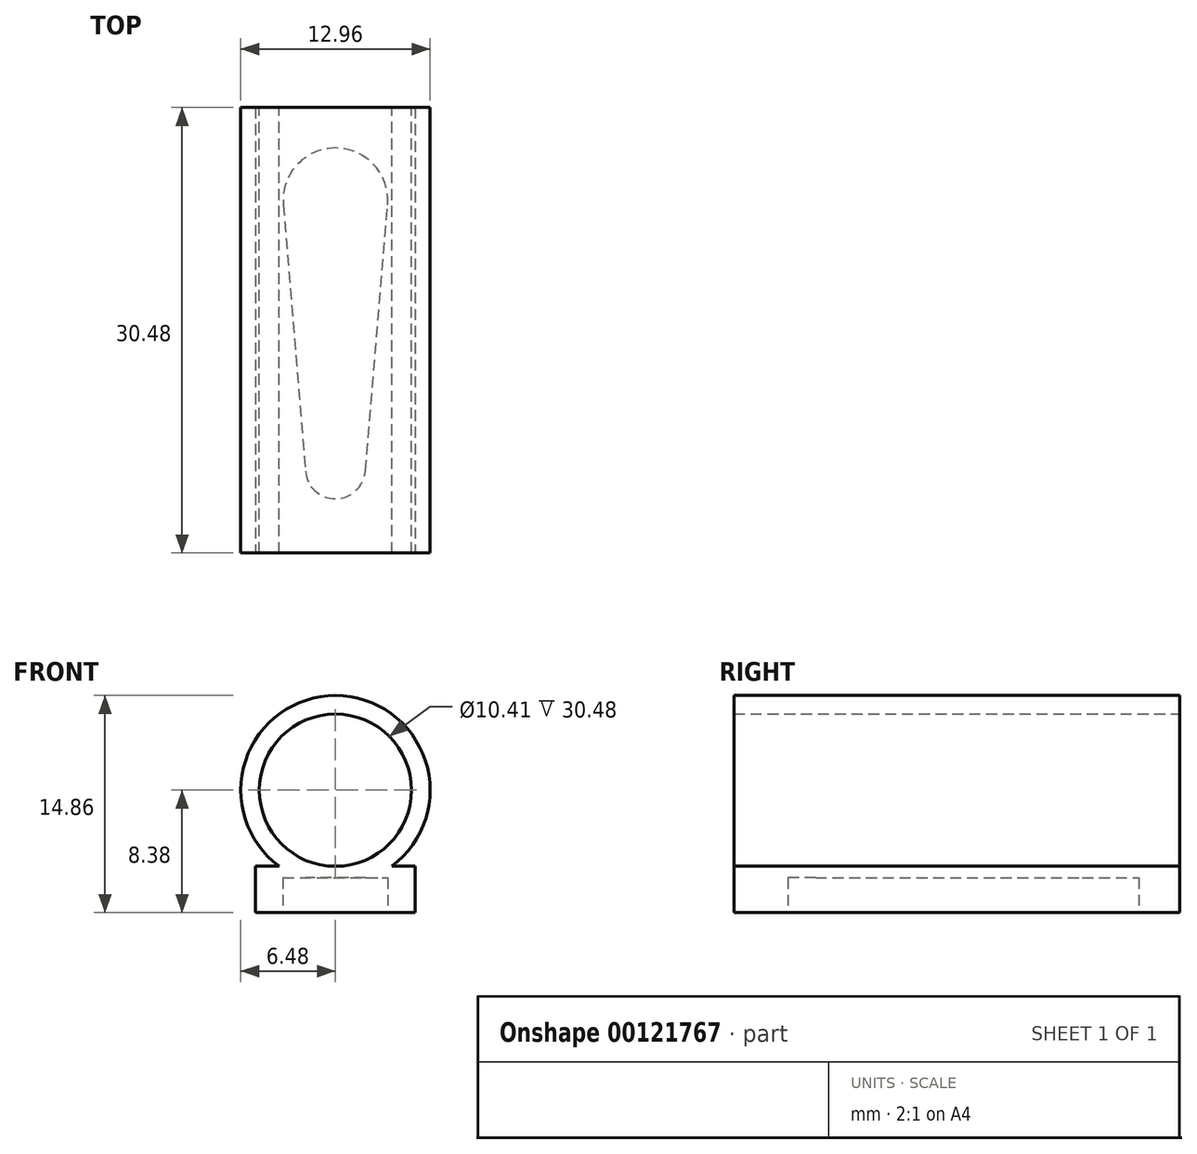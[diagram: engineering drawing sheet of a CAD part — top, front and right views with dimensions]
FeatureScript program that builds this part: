
annotation { "Feature Type Name" : "Feature", "Feature Type Description" : "" }
export const myFeature = defineFeature(function(context is Context, id is Id, definition is map)
    precondition{}
    {
        {
            var Q0;
            Q0=qCreatedBy(makeId("Front.planeOp"),FACE);
            var sketch = newSketch(context, id + "F0", { "sketchPlane" : qUnion([Q0])});
            skCircle(sketch, "E0", {"center": v(0, 0) * mm, "radius": 6.48 * mm});
            skSolve(sketch);
        }
        {
            var Q0;
            Q0 = qSketchRegion(id + "F0", true);
            extrude(context, id + "F1", {"entities" : qUnion([Q0]), "depth" : 30.48 * mm});
        }
        {
            var Q0;
            Q0=makeQuery(id+"F1.opExtrude","CAP_FACE",FACE,{"disambiguationData":[OSD([sQuery(id+"F0.wireOp",EDGE,"E0")])],"isStart":true});
            var sketch = newSketch(context, id + "F2", { "sketchPlane" : qUnion([Q0])});
            skCircle(sketch, "E1", {"center": v(0, 0) * mm, "radius": 5.2 * mm});
            skSolve(sketch);
        }
        {
            var Q0;
            Q0 = qSketchRegion(id + "F2", true);
            var Q1;
            Q1=makeQuery(id+"F1.opExtrude","CAP_FACE",FACE,{"disambiguationData":[OSD([sQuery(id+"F0.wireOp",EDGE,"E0")])],"isStart":false});
            extrude(context, id + "F3", {"entities" : qUnion([Q0]), "operationType" : NewBodyOperationType.REMOVE, "endBound" : BoundingType.UP_TO_SURFACE, "oppositeDirection" : true, "endBoundEntityFace" : qUnion([Q1]), "depth" : 25.4 * mm});
        }
        {
            var Q0;
            Q0=qCreatedBy(makeId("Top.planeOp"),FACE);
            cPlane(context, id + "F4", {"entities" : qUnion([Q0]), "cplaneType" : CPlaneType.OFFSET, "offset" : 5.2 * mm, "oppositeDirection" : true, "width" : 152.4 * mm, "height" : 152.4 * mm});
        }
        {
            var Q0;
            Q0=qCreatedBy(id+"F4.planeOp",FACE);
            var sketch = newSketch(context, id + "F5", { "sketchPlane" : qUnion([Q0])});
            skLineSegment(sketch, "E2.bottom", {"start": v(-5.46, 0) * mm, "end": v(5.46, 0) * mm});
            skLineSegment(sketch, "E2.top", {"start": v(-5.46, -30.48) * mm, "end": v(5.46, -30.48) * mm});
            skLineSegment(sketch, "E2.left", {"start": v(-5.46, 0) * mm, "end": v(-5.46, -30.48) * mm});
            skLineSegment(sketch, "E2.right", {"start": v(5.46, 0) * mm, "end": v(5.46, -30.48) * mm});
            skSolve(sketch);
        }
        {
            var Q0;
            Q0 = qSketchRegion(id + "F5", true);
            extrude(context, id + "F6", {"entities" : qUnion([Q0]), "operationType" : NewBodyOperationType.ADD, "oppositeDirection" : true, "depth" : 3.17 * mm});
        }
        {
            var Q0;
            Q0=makeQuery(id+"F6.opExtrude","CAP_FACE",FACE,{"disambiguationData":[OSD([sQuery(id+"F5.wireOp",EDGE,"E2.bottom"),sQuery(id+"F5.wireOp",EDGE,"E2.top"),sQuery(id+"F5.wireOp",EDGE,"E2.left"),sQuery(id+"F5.wireOp",EDGE,"E2.right")])],"isStart":false});
            var sketch = newSketch(context, id + "F7", { "sketchPlane" : qUnion([Q0])});
            skArc(sketch, "E3", {"start": v(-3.42, 6.63) * mm, "mid": v(0, 2.92) * mm, "end": v(3.42, 6.63) * mm, "construction": true});
            skArc(sketch, "E4", {"start": v(1.9, 24.87) * mm, "mid": v(0, 26.62) * mm, "end": v(-1.9, 24.87) * mm, "construction": true});
            skLineSegment(sketch, "E5", {"start": v(-3.42, 6.63) * mm, "end": v(-1.9, 24.87) * mm, "construction": true});
            skLineSegment(sketch, "E6", {"start": v(1.9, 24.87) * mm, "end": v(3.42, 6.63) * mm, "construction": true});
            skCircle(sketch, "E7", {"center": v(0, 6.35) * mm, "radius": 1.27 * mm});
            skLineSegment(sketch, "E8", {"start": v(0, 6.35) * mm, "end": v(0, 24.71) * mm, "construction": true});
            skArc(sketch, "E9.0", {"start": v(2.05, 24.88) * mm, "mid": v(0, 26.77) * mm, "end": v(-2.05, 24.88) * mm});
            skLineSegment(sketch, "E9.1", {"start": v(2.05, 24.88) * mm, "end": v(3.57, 6.65) * mm});
            skArc(sketch, "E9.2", {"start": v(-3.57, 6.65) * mm, "mid": v(0, 2.77) * mm, "end": v(3.57, 6.65) * mm});
            skLineSegment(sketch, "E10.0", {"start": v(-3.57, 6.65) * mm, "end": v(-2.05, 24.88) * mm});
            skSolve(sketch);
        }
        {
            var Q0;
            Q0=makeQuery(id+"F7.imprint","IMPRINT",FACE,{"disambiguationData":[TD([[makeQuery(id+"F7.imprint","IMPRINT",EDGE,{"derivedFrom":sQuery(id+"F7.wireOp",EDGE,"E7")}),-1.0]])]});
            var Q1;
            Q1=makeQuery(id+"F7.imprint","IMPRINT",FACE,{"disambiguationData":[TD([[makeQuery(id+"F7.imprint","IMPRINT",EDGE,{"derivedFrom":sQuery(id+"F7.wireOp",EDGE,"E7")}),1.0]])]});
            var Q2;
            Q2=makeQuery(id+"F3.boolean.opBoolean","COPY",FACE,{"derivedFrom":makeQuery(id+"F3.opExtrude","SWEPT_FACE",FACE,{"disambiguationData":[OSD([sQuery(id+"F2.wireOp",EDGE,"E1")])]})});
            extrude(context, id + "F8", {"entities" : qUnion([Q0, Q1]), "operationType" : NewBodyOperationType.REMOVE, "oppositeDirection" : true, "endBoundEntityFace" : qUnion([Q2]), "depth" : 2.38 * mm});
        }
    });
